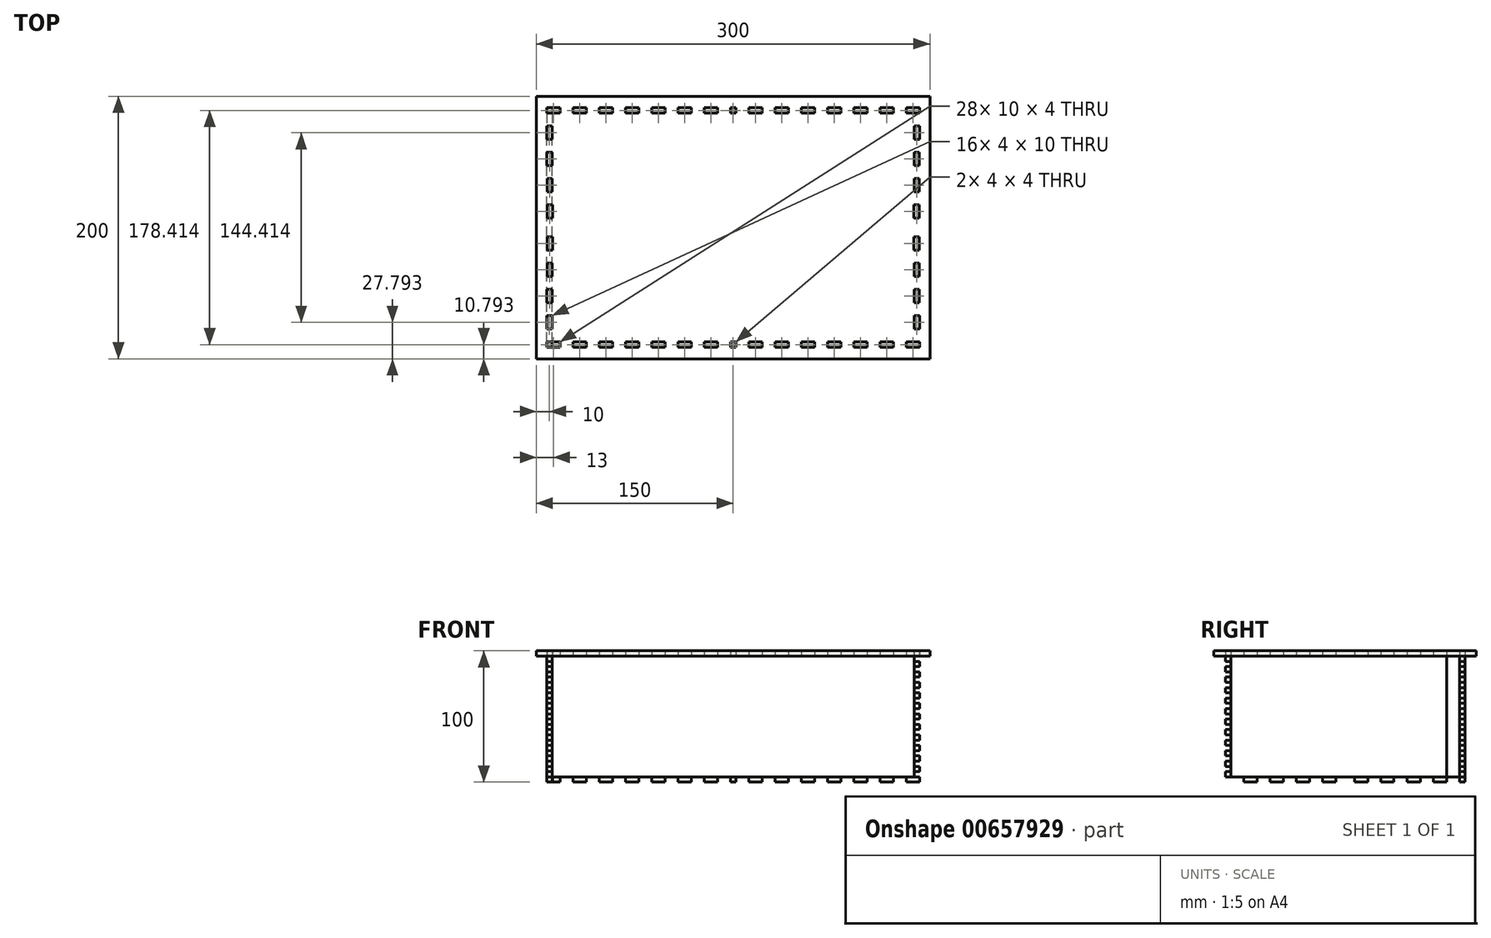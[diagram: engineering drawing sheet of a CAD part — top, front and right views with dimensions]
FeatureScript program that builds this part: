
annotation { "Feature Type Name" : "Feature", "Feature Type Description" : "" }
export const myFeature = defineFeature(function(context is Context, id is Id, definition is map)
    precondition{}
    {
        {
            assignVariable(context, id + "F0", {"name" : "width", "anyValue" : 4 * mm});
        }
        {
            var Q0;
            Q0=qCreatedBy(makeId("Top.planeOp"),FACE);
            var sketch = newSketch(context, id + "F1", { "sketchPlane" : qUnion([Q0])});
            skLineSegment(sketch, "E0.bottom", {"start": v(150, 100) * mm, "end": v(-150, 100) * mm});
            skLineSegment(sketch, "E0.top", {"start": v(150, -100) * mm, "end": v(-150, -100) * mm});
            skLineSegment(sketch, "E0.left", {"start": v(150, 100) * mm, "end": v(150, -100) * mm});
            skLineSegment(sketch, "E0.right", {"start": v(-150, 100) * mm, "end": v(-150, -100) * mm});
            skPoint(sketch, "E0.middle", {"position": v(0, 0) * mm});
            skLineSegment(sketch, "E1.bottom", {"start": v(-142, 87.2) * mm, "end": v(-132, 87.2) * mm});
            skLineSegment(sketch, "E1.top", {"start": v(-142, 91.2) * mm, "end": v(-132, 91.2) * mm});
            skLineSegment(sketch, "E1.left", {"start": v(-142, 87.2) * mm, "end": v(-142, 91.2) * mm});
            skLineSegment(sketch, "E1.right", {"start": v(-132, 87.2) * mm, "end": v(-132, 91.2) * mm});
            skLineSegment(sketch, "E2.1.0.0", {"start": v(-122, 91.2) * mm, "end": v(-112, 91.2) * mm});
            skLineSegment(sketch, "E2.1.0.1", {"start": v(-112, 87.2) * mm, "end": v(-112, 91.2) * mm});
            skLineSegment(sketch, "E2.1.0.2", {"start": v(-122, 87.2) * mm, "end": v(-122, 91.2) * mm});
            skLineSegment(sketch, "E2.1.0.3", {"start": v(-122, 87.2) * mm, "end": v(-112, 87.2) * mm});
            skLineSegment(sketch, "E2.2.0.0", {"start": v(-102, 91.2) * mm, "end": v(-92, 91.2) * mm});
            skLineSegment(sketch, "E2.2.0.1", {"start": v(-92, 87.2) * mm, "end": v(-92, 91.2) * mm});
            skLineSegment(sketch, "E2.2.0.2", {"start": v(-102, 87.2) * mm, "end": v(-102, 91.2) * mm});
            skLineSegment(sketch, "E2.2.0.3", {"start": v(-102, 87.2) * mm, "end": v(-92, 87.2) * mm});
            skLineSegment(sketch, "E2.3.0.0", {"start": v(-82, 91.2) * mm, "end": v(-72, 91.2) * mm});
            skLineSegment(sketch, "E2.3.0.1", {"start": v(-72, 87.2) * mm, "end": v(-72, 91.2) * mm});
            skLineSegment(sketch, "E2.3.0.2", {"start": v(-82, 87.2) * mm, "end": v(-82, 91.2) * mm});
            skLineSegment(sketch, "E2.3.0.3", {"start": v(-82, 87.2) * mm, "end": v(-72, 87.2) * mm});
            skLineSegment(sketch, "E2.4.0.0", {"start": v(-62, 91.2) * mm, "end": v(-52, 91.2) * mm});
            skLineSegment(sketch, "E2.4.0.1", {"start": v(-52, 87.2) * mm, "end": v(-52, 91.2) * mm});
            skLineSegment(sketch, "E2.4.0.2", {"start": v(-62, 87.2) * mm, "end": v(-62, 91.2) * mm});
            skLineSegment(sketch, "E2.4.0.3", {"start": v(-62, 87.2) * mm, "end": v(-52, 87.2) * mm});
            skLineSegment(sketch, "E2.5.0.0", {"start": v(-42, 91.2) * mm, "end": v(-32, 91.2) * mm});
            skLineSegment(sketch, "E2.5.0.1", {"start": v(-32, 87.2) * mm, "end": v(-32, 91.2) * mm});
            skLineSegment(sketch, "E2.5.0.2", {"start": v(-42, 87.2) * mm, "end": v(-42, 91.2) * mm});
            skLineSegment(sketch, "E2.5.0.3", {"start": v(-42, 87.2) * mm, "end": v(-32, 87.2) * mm});
            skLineSegment(sketch, "E2.6.0.0", {"start": v(-22, 91.2) * mm, "end": v(-12, 91.2) * mm});
            skLineSegment(sketch, "E2.6.0.1", {"start": v(-12, 87.2) * mm, "end": v(-12, 91.2) * mm});
            skLineSegment(sketch, "E2.6.0.2", {"start": v(-22, 87.2) * mm, "end": v(-22, 91.2) * mm});
            skLineSegment(sketch, "E2.6.0.3", {"start": v(-22, 87.2) * mm, "end": v(-12, 87.2) * mm});
            skLineSegment(sketch, "E2.7.0.0", {"start": v(-2, 91.2) * mm, "end": v(0, 91.2) * mm});
            skLineSegment(sketch, "E2.7.0.2", {"start": v(-2, 87.2) * mm, "end": v(-2, 91.2) * mm});
            skLineSegment(sketch, "E2.direction1", {"start": v(-142, 91.2) * mm, "end": v(-122, 91.2) * mm, "construction": true});
            skLineSegment(sketch, "E3", {"start": v(0, 0) * mm, "end": v(0, 100) * mm, "construction": true});
            skLineSegment(sketch, "E4", {"start": v(0, 0) * mm, "end": v(0, -100) * mm, "construction": true});
            skLineSegment(sketch, "E5.MirrorCS", {"start": v(142, 91.2) * mm, "end": v(132, 91.2) * mm});
            skLineSegment(sketch, "E6.MirrorCS", {"start": v(142, 87.2) * mm, "end": v(142, 91.2) * mm});
            skLineSegment(sketch, "E7.MirrorCS", {"start": v(142, 87.2) * mm, "end": v(132, 87.2) * mm});
            skLineSegment(sketch, "E8.MirrorCS", {"start": v(132, 87.2) * mm, "end": v(132, 91.2) * mm});
            skLineSegment(sketch, "E9.MirrorCS", {"start": v(62, 87.2) * mm, "end": v(62, 91.2) * mm});
            skLineSegment(sketch, "E10.MirrorCS", {"start": v(62, 91.2) * mm, "end": v(52, 91.2) * mm});
            skLineSegment(sketch, "E11.MirrorCS", {"start": v(52, 87.2) * mm, "end": v(52, 91.2) * mm});
            skLineSegment(sketch, "E12.MirrorCS", {"start": v(42, 87.2) * mm, "end": v(42, 91.2) * mm});
            skLineSegment(sketch, "E13.MirrorCS", {"start": v(42, 91.2) * mm, "end": v(32, 91.2) * mm});
            skLineSegment(sketch, "E14.MirrorCS", {"start": v(32, 87.2) * mm, "end": v(32, 91.2) * mm});
            skLineSegment(sketch, "E15.MirrorCS", {"start": v(2, 87.2) * mm, "end": v(2, 91.2) * mm});
            skLineSegment(sketch, "E16.MirrorCS", {"start": v(2, 91.2) * mm, "end": v(0, 91.2) * mm});
            skLineSegment(sketch, "E17.MirrorCS", {"start": v(12, 87.2) * mm, "end": v(12, 91.2) * mm});
            skLineSegment(sketch, "E18.MirrorCS", {"start": v(22, 87.2) * mm, "end": v(22, 91.2) * mm});
            skLineSegment(sketch, "E19.MirrorCS", {"start": v(22, 91.2) * mm, "end": v(12, 91.2) * mm});
            skLineSegment(sketch, "E20.MirrorCS", {"start": v(82, 91.2) * mm, "end": v(72, 91.2) * mm});
            skLineSegment(sketch, "E21.MirrorCS", {"start": v(102, 91.2) * mm, "end": v(92, 91.2) * mm});
            skLineSegment(sketch, "E22.MirrorCS", {"start": v(92, 87.2) * mm, "end": v(92, 91.2) * mm});
            skLineSegment(sketch, "E23.MirrorCS", {"start": v(102, 87.2) * mm, "end": v(102, 91.2) * mm});
            skLineSegment(sketch, "E24.MirrorCS", {"start": v(72, 87.2) * mm, "end": v(72, 91.2) * mm});
            skLineSegment(sketch, "E25.MirrorCS", {"start": v(82, 87.2) * mm, "end": v(82, 91.2) * mm});
            skLineSegment(sketch, "E26.MirrorCS", {"start": v(112, 87.2) * mm, "end": v(112, 91.2) * mm});
            skLineSegment(sketch, "E27.MirrorCS", {"start": v(122, 91.2) * mm, "end": v(112, 91.2) * mm});
            skLineSegment(sketch, "E28.MirrorCS", {"start": v(122, 87.2) * mm, "end": v(122, 91.2) * mm});
            skLineSegment(sketch, "E29", {"start": v(2, 87.2) * mm, "end": v(-2, 87.2) * mm});
            skLineSegment(sketch, "E30.MirrorCS", {"start": v(22, 87.2) * mm, "end": v(12, 87.2) * mm});
            skLineSegment(sketch, "E31.MirrorCS", {"start": v(102, 87.2) * mm, "end": v(92, 87.2) * mm});
            skLineSegment(sketch, "E32.MirrorCS", {"start": v(62, 87.2) * mm, "end": v(52, 87.2) * mm});
            skLineSegment(sketch, "E33.MirrorCS", {"start": v(82, 87.2) * mm, "end": v(72, 87.2) * mm});
            skLineSegment(sketch, "E34.MirrorCS", {"start": v(42, 87.2) * mm, "end": v(32, 87.2) * mm});
            skLineSegment(sketch, "E35.MirrorCS", {"start": v(122, 87.2) * mm, "end": v(112, 87.2) * mm});
            skLineSegment(sketch, "E36", {"start": v(150, 0) * mm, "end": v(-150, 0) * mm, "construction": true});
            skLineSegment(sketch, "E37.MirrorCS", {"start": v(42, -87.2) * mm, "end": v(42, -91.2) * mm});
            skLineSegment(sketch, "E38.MirrorCS", {"start": v(52, -87.2) * mm, "end": v(52, -91.2) * mm});
            skLineSegment(sketch, "E39.MirrorCS", {"start": v(32, -87.2) * mm, "end": v(32, -91.2) * mm});
            skLineSegment(sketch, "E40.MirrorCS", {"start": v(62, -87.2) * mm, "end": v(62, -91.2) * mm});
            skLineSegment(sketch, "E41.MirrorCS", {"start": v(92, -87.2) * mm, "end": v(92, -91.2) * mm});
            skLineSegment(sketch, "E42.MirrorCS", {"start": v(102, -87.2) * mm, "end": v(102, -91.2) * mm});
            skLineSegment(sketch, "E43.MirrorCS", {"start": v(132, -87.2) * mm, "end": v(132, -91.2) * mm});
            skLineSegment(sketch, "E44.MirrorCS", {"start": v(12, -87.2) * mm, "end": v(12, -91.2) * mm});
            skLineSegment(sketch, "E45.MirrorCS", {"start": v(72, -87.2) * mm, "end": v(72, -91.2) * mm});
            skLineSegment(sketch, "E46.MirrorCS", {"start": v(82, -87.2) * mm, "end": v(82, -91.2) * mm});
            skLineSegment(sketch, "E47.MirrorCS", {"start": v(22, -87.2) * mm, "end": v(22, -91.2) * mm});
            skLineSegment(sketch, "E48.MirrorCS", {"start": v(42, -91.2) * mm, "end": v(32, -91.2) * mm});
            skLineSegment(sketch, "E49.MirrorCS", {"start": v(-142, -87.2) * mm, "end": v(-142, -91.2) * mm});
            skLineSegment(sketch, "E50.MirrorCS", {"start": v(-122, -87.2) * mm, "end": v(-122, -91.2) * mm});
            skLineSegment(sketch, "E51.MirrorCS", {"start": v(-42, -87.2) * mm, "end": v(-42, -91.2) * mm});
            skLineSegment(sketch, "E52.MirrorCS", {"start": v(112, -87.2) * mm, "end": v(112, -91.2) * mm});
            skLineSegment(sketch, "E53.MirrorCS", {"start": v(-32, -87.2) * mm, "end": v(-32, -91.2) * mm});
            skLineSegment(sketch, "E54.MirrorCS", {"start": v(2, -87.2) * mm, "end": v(-2, -87.2) * mm});
            skLineSegment(sketch, "E55.MirrorCS", {"start": v(-12, -87.2) * mm, "end": v(-12, -91.2) * mm});
            skLineSegment(sketch, "E56.MirrorCS", {"start": v(-142, -91.2) * mm, "end": v(-132, -91.2) * mm});
            skLineSegment(sketch, "E57.MirrorCS", {"start": v(-2, -87.2) * mm, "end": v(-2, -91.2) * mm});
            skLineSegment(sketch, "E58.MirrorCS", {"start": v(-72, -87.2) * mm, "end": v(-72, -91.2) * mm});
            skLineSegment(sketch, "E59.MirrorCS", {"start": v(-132, -87.2) * mm, "end": v(-132, -91.2) * mm});
            skLineSegment(sketch, "E60.MirrorCS", {"start": v(-92, -87.2) * mm, "end": v(-92, -91.2) * mm});
            skLineSegment(sketch, "E61.MirrorCS", {"start": v(-52, -87.2) * mm, "end": v(-52, -91.2) * mm});
            skLineSegment(sketch, "E62.MirrorCS", {"start": v(-112, -87.2) * mm, "end": v(-112, -91.2) * mm});
            skLineSegment(sketch, "E63.MirrorCS", {"start": v(62, -91.2) * mm, "end": v(52, -91.2) * mm});
            skLineSegment(sketch, "E64.MirrorCS", {"start": v(-102, -87.2) * mm, "end": v(-102, -91.2) * mm});
            skLineSegment(sketch, "E65.MirrorCS", {"start": v(-82, -87.2) * mm, "end": v(-82, -91.2) * mm});
            skLineSegment(sketch, "E66.MirrorCS", {"start": v(2, -91.2) * mm, "end": v(0, -91.2) * mm});
            skLineSegment(sketch, "E67.MirrorCS", {"start": v(-62, -87.2) * mm, "end": v(-62, -91.2) * mm});
            skLineSegment(sketch, "E68.MirrorCS", {"start": v(-2, -91.2) * mm, "end": v(0, -91.2) * mm});
            skLineSegment(sketch, "E69.MirrorCS", {"start": v(122, -87.2) * mm, "end": v(122, -91.2) * mm});
            skLineSegment(sketch, "E70.MirrorCS", {"start": v(2, -87.2) * mm, "end": v(2, -91.2) * mm});
            skLineSegment(sketch, "E71.MirrorCS", {"start": v(-22, -87.2) * mm, "end": v(-22, -91.2) * mm});
            skLineSegment(sketch, "E72.MirrorCS", {"start": v(102, -91.2) * mm, "end": v(92, -91.2) * mm});
            skLineSegment(sketch, "E73.MirrorCS", {"start": v(-142, -91.2) * mm, "end": v(-122, -91.2) * mm, "construction": true});
            skLineSegment(sketch, "E74.MirrorCS", {"start": v(22, -91.2) * mm, "end": v(12, -91.2) * mm});
            skLineSegment(sketch, "E75.MirrorCS", {"start": v(82, -91.2) * mm, "end": v(72, -91.2) * mm});
            skLineSegment(sketch, "E76.MirrorCS", {"start": v(142, -91.2) * mm, "end": v(132, -91.2) * mm});
            skLineSegment(sketch, "E77.MirrorCS", {"start": v(-142, -87.2) * mm, "end": v(-132, -87.2) * mm});
            skLineSegment(sketch, "E78.MirrorCS", {"start": v(142, -87.2) * mm, "end": v(142, -91.2) * mm});
            skLineSegment(sketch, "E79.MirrorCS", {"start": v(142, -87.2) * mm, "end": v(132, -87.2) * mm});
            skLineSegment(sketch, "E80.MirrorCS", {"start": v(-82, -87.2) * mm, "end": v(-72, -87.2) * mm});
            skLineSegment(sketch, "E81.MirrorCS", {"start": v(82, -87.2) * mm, "end": v(72, -87.2) * mm});
            skLineSegment(sketch, "E82.MirrorCS", {"start": v(42, -87.2) * mm, "end": v(32, -87.2) * mm});
            skLineSegment(sketch, "E83.MirrorCS", {"start": v(122, -91.2) * mm, "end": v(112, -91.2) * mm});
            skLineSegment(sketch, "E84.MirrorCS", {"start": v(-62, -91.2) * mm, "end": v(-52, -91.2) * mm});
            skLineSegment(sketch, "E85.MirrorCS", {"start": v(122, -87.2) * mm, "end": v(112, -87.2) * mm});
            skLineSegment(sketch, "E86.MirrorCS", {"start": v(-42, -87.2) * mm, "end": v(-32, -87.2) * mm});
            skLineSegment(sketch, "E87.MirrorCS", {"start": v(-122, -91.2) * mm, "end": v(-112, -91.2) * mm});
            skLineSegment(sketch, "E88.MirrorCS", {"start": v(-102, -87.2) * mm, "end": v(-92, -87.2) * mm});
            skLineSegment(sketch, "E89.MirrorCS", {"start": v(-22, -87.2) * mm, "end": v(-12, -87.2) * mm});
            skLineSegment(sketch, "E90.MirrorCS", {"start": v(-102, -91.2) * mm, "end": v(-92, -91.2) * mm});
            skLineSegment(sketch, "E91.MirrorCS", {"start": v(-42, -91.2) * mm, "end": v(-32, -91.2) * mm});
            skLineSegment(sketch, "E92.MirrorCS", {"start": v(102, -87.2) * mm, "end": v(92, -87.2) * mm});
            skLineSegment(sketch, "E93.MirrorCS", {"start": v(-22, -91.2) * mm, "end": v(-12, -91.2) * mm});
            skLineSegment(sketch, "E94.MirrorCS", {"start": v(62, -87.2) * mm, "end": v(52, -87.2) * mm});
            skLineSegment(sketch, "E95.MirrorCS", {"start": v(-62, -87.2) * mm, "end": v(-52, -87.2) * mm});
            skLineSegment(sketch, "E96.MirrorCS", {"start": v(22, -87.2) * mm, "end": v(12, -87.2) * mm});
            skLineSegment(sketch, "E97.MirrorCS", {"start": v(-82, -91.2) * mm, "end": v(-72, -91.2) * mm});
            skLineSegment(sketch, "E98.MirrorCS", {"start": v(-122, -87.2) * mm, "end": v(-112, -87.2) * mm});
            skLineSegment(sketch, "E99.bottom", {"start": v(142, 77.2) * mm, "end": v(138, 77.2) * mm});
            skLineSegment(sketch, "E99.top", {"start": v(142, 67.2) * mm, "end": v(138, 67.2) * mm});
            skLineSegment(sketch, "E99.left", {"start": v(142, 77.2) * mm, "end": v(142, 67.2) * mm});
            skLineSegment(sketch, "E99.right", {"start": v(138, 77.2) * mm, "end": v(138, 67.2) * mm});
            skLineSegment(sketch, "E100.1.0.0", {"start": v(141.92, 47.2) * mm, "end": v(137.92, 47.2) * mm});
            skLineSegment(sketch, "E100.1.0.1", {"start": v(137.92, 57.2) * mm, "end": v(137.92, 47.2) * mm});
            skLineSegment(sketch, "E100.1.0.2", {"start": v(141.92, 57.2) * mm, "end": v(141.92, 47.2) * mm});
            skLineSegment(sketch, "E100.1.0.3", {"start": v(141.92, 57.2) * mm, "end": v(137.92, 57.2) * mm});
            skLineSegment(sketch, "E100.2.0.0", {"start": v(141.84, 27.2) * mm, "end": v(137.84, 27.2) * mm});
            skLineSegment(sketch, "E100.2.0.1", {"start": v(137.84, 37.2) * mm, "end": v(137.84, 27.2) * mm});
            skLineSegment(sketch, "E100.2.0.2", {"start": v(141.84, 37.2) * mm, "end": v(141.84, 27.2) * mm});
            skLineSegment(sketch, "E100.2.0.3", {"start": v(141.84, 37.2) * mm, "end": v(137.84, 37.2) * mm});
            skLineSegment(sketch, "E100.direction1", {"start": v(138, 67.2) * mm, "end": v(137.92, 47.2) * mm, "construction": true});
            skLineSegment(sketch, "E101.MirrorCS", {"start": v(141.84, -37.2) * mm, "end": v(141.84, -27.2) * mm});
            skLineSegment(sketch, "E102.MirrorCS", {"start": v(141.84, -37.2) * mm, "end": v(137.84, -37.2) * mm});
            skLineSegment(sketch, "E103.MirrorCS", {"start": v(137.84, -37.2) * mm, "end": v(137.84, -27.2) * mm});
            skLineSegment(sketch, "E104.MirrorCS", {"start": v(141.84, -27.2) * mm, "end": v(137.84, -27.2) * mm});
            skLineSegment(sketch, "E105.MirrorCS", {"start": v(141.92, -47.2) * mm, "end": v(137.92, -47.2) * mm});
            skLineSegment(sketch, "E106.MirrorCS", {"start": v(141.92, -57.2) * mm, "end": v(141.92, -47.2) * mm});
            skLineSegment(sketch, "E107.MirrorCS", {"start": v(141.92, -57.2) * mm, "end": v(137.92, -57.2) * mm});
            skLineSegment(sketch, "E108.MirrorCS", {"start": v(142, -67.2) * mm, "end": v(138, -67.2) * mm});
            skLineSegment(sketch, "E109.MirrorCS", {"start": v(142, -77.2) * mm, "end": v(142, -67.2) * mm});
            skLineSegment(sketch, "E110.MirrorCS", {"start": v(142, -77.2) * mm, "end": v(138, -77.2) * mm});
            skLineSegment(sketch, "E111.MirrorCS", {"start": v(138, -77.2) * mm, "end": v(138, -67.2) * mm});
            skLineSegment(sketch, "E112.MirrorCS", {"start": v(137.92, -57.2) * mm, "end": v(137.92, -47.2) * mm});
            skLineSegment(sketch, "E113.0.3.0", {"start": v(141.75, 7.2) * mm, "end": v(137.75, 7.2) * mm});
            skLineSegment(sketch, "E113.3.3.0", {"start": v(137.75, 17.2) * mm, "end": v(137.75, 7.2) * mm});
            skLineSegment(sketch, "E113.6.3.0", {"start": v(141.75, 17.2) * mm, "end": v(141.75, 7.2) * mm});
            skLineSegment(sketch, "E113.9.3.0", {"start": v(141.75, 17.2) * mm, "end": v(137.75, 17.2) * mm});
            skLineSegment(sketch, "E114.MirrorCS", {"start": v(141.75, -7.2) * mm, "end": v(137.75, -7.2) * mm});
            skLineSegment(sketch, "E115.MirrorCS", {"start": v(141.75, -17.2) * mm, "end": v(141.75, -7.2) * mm});
            skLineSegment(sketch, "E116.MirrorCS", {"start": v(137.75, -17.2) * mm, "end": v(137.75, -7.2) * mm});
            skLineSegment(sketch, "E117.MirrorCS", {"start": v(141.75, -17.2) * mm, "end": v(137.75, -17.2) * mm});
            skLineSegment(sketch, "E118", {"start": v(0, 100) * mm, "end": v(0, -100) * mm, "construction": true});
            skLineSegment(sketch, "E119.MirrorCS", {"start": v(-138, 77.2) * mm, "end": v(-138, 67.2) * mm});
            skLineSegment(sketch, "E120.MirrorCS", {"start": v(-142, 77.2) * mm, "end": v(-138, 77.2) * mm});
            skLineSegment(sketch, "E121.MirrorCS", {"start": v(-142, 77.2) * mm, "end": v(-142, 67.2) * mm});
            skLineSegment(sketch, "E122.MirrorCS", {"start": v(-142, 67.2) * mm, "end": v(-138, 67.2) * mm});
            skLineSegment(sketch, "E123.MirrorCS", {"start": v(-141.92, 57.2) * mm, "end": v(-141.92, 47.2) * mm});
            skLineSegment(sketch, "E124.MirrorCS", {"start": v(-137.92, 57.2) * mm, "end": v(-137.92, 47.2) * mm});
            skLineSegment(sketch, "E125.MirrorCS", {"start": v(-141.92, 57.2) * mm, "end": v(-137.92, 57.2) * mm});
            skLineSegment(sketch, "E126.MirrorCS", {"start": v(-141.92, 47.2) * mm, "end": v(-137.92, 47.2) * mm});
            skLineSegment(sketch, "E127.MirrorCS", {"start": v(-141.84, 37.2) * mm, "end": v(-137.84, 37.2) * mm});
            skLineSegment(sketch, "E128.MirrorCS", {"start": v(-141.84, 37.2) * mm, "end": v(-141.84, 27.2) * mm});
            skLineSegment(sketch, "E129.MirrorCS", {"start": v(-137.84, 37.2) * mm, "end": v(-137.84, 27.2) * mm});
            skLineSegment(sketch, "E130.MirrorCS", {"start": v(-141.84, 27.2) * mm, "end": v(-137.84, 27.2) * mm});
            skLineSegment(sketch, "E131.MirrorCS", {"start": v(-141.75, 17.2) * mm, "end": v(-137.75, 17.2) * mm});
            skLineSegment(sketch, "E132.MirrorCS", {"start": v(-137.75, 17.2) * mm, "end": v(-137.75, 7.2) * mm});
            skLineSegment(sketch, "E133.MirrorCS", {"start": v(-141.75, 17.2) * mm, "end": v(-141.75, 7.2) * mm});
            skLineSegment(sketch, "E134.MirrorCS", {"start": v(-141.75, 7.2) * mm, "end": v(-137.75, 7.2) * mm});
            skLineSegment(sketch, "E135.MirrorCS", {"start": v(-141.75, -17.2) * mm, "end": v(-137.75, -17.2) * mm});
            skLineSegment(sketch, "E136.MirrorCS", {"start": v(-142, -67.2) * mm, "end": v(-138, -67.2) * mm});
            skLineSegment(sketch, "E137.MirrorCS", {"start": v(-142, -77.2) * mm, "end": v(-138, -77.2) * mm});
            skLineSegment(sketch, "E138.MirrorCS", {"start": v(-141.92, -57.2) * mm, "end": v(-137.92, -57.2) * mm});
            skLineSegment(sketch, "E139.MirrorCS", {"start": v(-141.84, -27.2) * mm, "end": v(-137.84, -27.2) * mm});
            skLineSegment(sketch, "E140.MirrorCS", {"start": v(-141.75, -7.2) * mm, "end": v(-137.75, -7.2) * mm});
            skLineSegment(sketch, "E141.MirrorCS", {"start": v(-141.92, -47.2) * mm, "end": v(-137.92, -47.2) * mm});
            skLineSegment(sketch, "E142.MirrorCS", {"start": v(-141.84, -37.2) * mm, "end": v(-137.84, -37.2) * mm});
            skLineSegment(sketch, "E143.MirrorCS", {"start": v(-141.92, -57.2) * mm, "end": v(-141.92, -47.2) * mm});
            skLineSegment(sketch, "E144.MirrorCS", {"start": v(-142, -77.2) * mm, "end": v(-142, -67.2) * mm});
            skLineSegment(sketch, "E145.MirrorCS", {"start": v(-141.84, -37.2) * mm, "end": v(-141.84, -27.2) * mm});
            skLineSegment(sketch, "E146.MirrorCS", {"start": v(-137.84, -37.2) * mm, "end": v(-137.84, -27.2) * mm});
            skLineSegment(sketch, "E147.MirrorCS", {"start": v(-141.75, -17.2) * mm, "end": v(-141.75, -7.2) * mm});
            skLineSegment(sketch, "E148.MirrorCS", {"start": v(-138, -77.2) * mm, "end": v(-138, -67.2) * mm});
            skLineSegment(sketch, "E149.MirrorCS", {"start": v(-137.92, -57.2) * mm, "end": v(-137.92, -47.2) * mm});
            skLineSegment(sketch, "E150.MirrorCS", {"start": v(-137.75, -17.2) * mm, "end": v(-137.75, -7.2) * mm});
            skLineSegment(sketch, "E151", {"start": v(-138, 87.2) * mm, "end": v(-138, 91.2) * mm});
            skPoint(sketch, "E151.endSnap0", {"position": v(-137, 91.2) * mm});
            skSolve(sketch);
        }
        {
            var Q0;
            Q0=makeQuery(id+"F1.imprint","IMPRINT",FACE,{"disambiguationData":[TD([[makeQuery(id+"F1.imprint","IMPRINT",EDGE,{"derivedFrom":sQuery(id+"F1.wireOp",EDGE,"E0.bottom")}),1.0]])]});
            extrude(context, id + "F2", {"entities" : qUnion([Q0]), "depth" : 4 * mm});
        }
        {
            var Q0;
            Q0=makeQuery(id+"F1.imprint","IMPRINT",FACE,{"disambiguationData":[TD([[makeQuery(id+"F1.imprint","IMPRINT",EDGE,{"derivedFrom":sQuery(id+"F1.wireOp",EDGE,"E20.MirrorCS")}),1.0]])]});
            var Q1;
            Q1=makeQuery(id+"F1.imprint","IMPRINT",FACE,{"disambiguationData":[TD([[makeQuery(id+"F1.imprint","IMPRINT",EDGE,{"derivedFrom":sQuery(id+"F1.wireOp",EDGE,"E13.MirrorCS")}),1.0]])]});
            var Q2;
            Q2=makeQuery(id+"F1.imprint","IMPRINT",FACE,{"disambiguationData":[TD([[makeQuery(id+"F1.imprint","IMPRINT",EDGE,{"derivedFrom":sQuery(id+"F1.wireOp",EDGE,"E1.bottom")}),1.0]])]});
            var Q3;
            Q3=makeQuery(id+"F1.imprint","IMPRINT",FACE,{"disambiguationData":[TD([[makeQuery(id+"F1.imprint","IMPRINT",EDGE,{"derivedFrom":sQuery(id+"F1.wireOp",EDGE,"E2.1.0.0")}),-1.0]])]});
            var Q4;
            Q4=makeQuery(id+"F1.imprint","IMPRINT",FACE,{"disambiguationData":[TD([[makeQuery(id+"F1.imprint","IMPRINT",EDGE,{"derivedFrom":sQuery(id+"F1.wireOp",EDGE,"E2.2.0.0")}),-1.0]])]});
            var Q5;
            Q5=makeQuery(id+"F1.imprint","IMPRINT",FACE,{"disambiguationData":[TD([[makeQuery(id+"F1.imprint","IMPRINT",EDGE,{"derivedFrom":sQuery(id+"F1.wireOp",EDGE,"E2.3.0.0")}),-1.0]])]});
            var Q6;
            Q6=makeQuery(id+"F1.imprint","IMPRINT",FACE,{"disambiguationData":[TD([[makeQuery(id+"F1.imprint","IMPRINT",EDGE,{"derivedFrom":sQuery(id+"F1.wireOp",EDGE,"E2.4.0.0")}),-1.0]])]});
            var Q7;
            Q7=makeQuery(id+"F1.imprint","IMPRINT",FACE,{"disambiguationData":[TD([[makeQuery(id+"F1.imprint","IMPRINT",EDGE,{"derivedFrom":sQuery(id+"F1.wireOp",EDGE,"E2.5.0.0")}),-1.0]])]});
            var Q8;
            Q8=makeQuery(id+"F1.imprint","IMPRINT",FACE,{"disambiguationData":[TD([[makeQuery(id+"F1.imprint","IMPRINT",EDGE,{"derivedFrom":sQuery(id+"F1.wireOp",EDGE,"E2.6.0.0")}),-1.0]])]});
            var Q9;
            Q9=makeQuery(id+"F1.imprint","IMPRINT",FACE,{"disambiguationData":[TD([[makeQuery(id+"F1.imprint","IMPRINT",EDGE,{"derivedFrom":sQuery(id+"F1.wireOp",EDGE,"E6.MirrorCS")}),1.0]])]});
            var Q10;
            Q10=makeQuery(id+"F1.imprint","IMPRINT",FACE,{"disambiguationData":[TD([[makeQuery(id+"F1.imprint","IMPRINT",EDGE,{"derivedFrom":sQuery(id+"F1.wireOp",EDGE,"E26.MirrorCS")}),-1.0]])]});
            var Q11;
            Q11=makeQuery(id+"F1.imprint","IMPRINT",FACE,{"disambiguationData":[TD([[makeQuery(id+"F1.imprint","IMPRINT",EDGE,{"derivedFrom":sQuery(id+"F1.wireOp",EDGE,"E30.MirrorCS")}),-1.0]])]});
            var Q12;
            Q12=makeQuery(id+"F1.imprint","IMPRINT",FACE,{"disambiguationData":[TD([[makeQuery(id+"F1.imprint","IMPRINT",EDGE,{"derivedFrom":sQuery(id+"F1.wireOp",EDGE,"E31.MirrorCS")}),-1.0]])]});
            var Q13;
            Q13=makeQuery(id+"F1.imprint","IMPRINT",FACE,{"disambiguationData":[TD([[makeQuery(id+"F1.imprint","IMPRINT",EDGE,{"derivedFrom":sQuery(id+"F1.wireOp",EDGE,"E32.MirrorCS")}),-1.0]])]});
            var Q14;
            Q14=makeQuery(id+"F1.imprint","IMPRINT",FACE,{"disambiguationData":[TD([[makeQuery(id+"F1.imprint","IMPRINT",EDGE,{"derivedFrom":sQuery(id+"F1.wireOp",EDGE,"E2.7.0.0")}),-1.0]])]});
            extrude(context, id + "F3", {"entities" : qUnion([Q0, Q1, Q2, Q3, Q4, Q5, Q6, Q7, Q8, Q9, Q10, Q11, Q12, Q13, Q14]), "depth" : 4 * mm});
        }
        {
            var Q0;
            Q0=sQuery(id+"F1.wireOp",EDGE,"E151");
            extrude(context, id + "F4", {"bodyType" : ToolBodyType.SURFACE, "surfaceEntities" : qUnion([Q0]), "oppositeDirection" : true, "depth" : 92 * mm});
        }
        {
            var Q0;
            Q0=makeQuery(id+"F4.opExtrude","SWEPT_FACE",FACE,{"disambiguationData":[OSD([sQuery(id+"F1.wireOp",EDGE,"E151")])]});
            extrude(context, id + "F5", {"entities" : qUnion([Q0]), "oppositeDirection" : true, "depth" : 276 * mm});
        }
        {
            var Q0;
            Q0=makeQuery(id+"F1.imprint","IMPRINT",FACE,{"disambiguationData":[TD([[makeQuery(id+"F1.imprint","IMPRINT",EDGE,{"derivedFrom":sQuery(id+"F1.wireOp",EDGE,"E127.MirrorCS")}),-1.0]])]});
            var Q1;
            Q1=makeQuery(id+"F1.imprint","IMPRINT",FACE,{"disambiguationData":[TD([[makeQuery(id+"F1.imprint","IMPRINT",EDGE,{"derivedFrom":sQuery(id+"F1.wireOp",EDGE,"E123.MirrorCS")}),1.0]])]});
            var Q2;
            Q2=makeQuery(id+"F1.imprint","IMPRINT",FACE,{"disambiguationData":[TD([[makeQuery(id+"F1.imprint","IMPRINT",EDGE,{"derivedFrom":sQuery(id+"F1.wireOp",EDGE,"E119.MirrorCS")}),-1.0]])]});
            var Q3;
            Q3=makeQuery(id+"F1.imprint","IMPRINT",FACE,{"disambiguationData":[TD([[makeQuery(id+"F1.imprint","IMPRINT",EDGE,{"derivedFrom":sQuery(id+"F1.wireOp",EDGE,"E131.MirrorCS")}),-1.0]])]});
            var Q4;
            Q4=makeQuery(id+"F1.imprint","IMPRINT",FACE,{"disambiguationData":[TD([[makeQuery(id+"F1.imprint","IMPRINT",EDGE,{"derivedFrom":sQuery(id+"F1.wireOp",EDGE,"E138.MirrorCS")}),1.0]])]});
            var Q5;
            Q5=makeQuery(id+"F1.imprint","IMPRINT",FACE,{"disambiguationData":[TD([[makeQuery(id+"F1.imprint","IMPRINT",EDGE,{"derivedFrom":sQuery(id+"F1.wireOp",EDGE,"E136.MirrorCS")}),-1.0]])]});
            var Q6;
            Q6=makeQuery(id+"F1.imprint","IMPRINT",FACE,{"disambiguationData":[TD([[makeQuery(id+"F1.imprint","IMPRINT",EDGE,{"derivedFrom":sQuery(id+"F1.wireOp",EDGE,"E139.MirrorCS")}),-1.0]])]});
            var Q7;
            Q7=makeQuery(id+"F1.imprint","IMPRINT",FACE,{"disambiguationData":[TD([[makeQuery(id+"F1.imprint","IMPRINT",EDGE,{"derivedFrom":sQuery(id+"F1.wireOp",EDGE,"E135.MirrorCS")}),1.0]])]});
            extrude(context, id + "F6", {"entities" : qUnion([Q0, Q1, Q2, Q3, Q4, Q5, Q6, Q7]), "depth" : 4 * mm});
        }
        {
            var Q0;
            Q0=sQuery(id+"F1.wireOp",EDGE,"E120.MirrorCS");
            extrude(context, id + "F7", {"bodyType" : ToolBodyType.SURFACE, "surfaceEntities" : qUnion([Q0]), "oppositeDirection" : true, "depth" : 92 * mm});
        }
        {
            var Q0;
            Q0=makeQuery(id+"F7.opExtrude","SWEPT_FACE",FACE,{"disambiguationData":[OSD([sQuery(id+"F1.wireOp",EDGE,"E120.MirrorCS")])]});
            extrude(context, id + "F8", {"entities" : qUnion([Q0]), "oppositeDirection" : true, "depth" : 164.42 * mm});
        }
        {
            var Q0;
            Q0=makeQuery(id+"F7.opExtrude","SWEPT_FACE",FACE,{"disambiguationData":[OSD([sQuery(id+"F1.wireOp",EDGE,"E120.MirrorCS")])]});
            extrude(context, id + "F9", {"entities" : qUnion([Q0]), "depth" : 10 * mm});
        }
        {
            var Q0;
            Q0=makeQuery(id+"F1.imprint","IMPRINT",FACE,{"disambiguationData":[TD([[makeQuery(id+"F1.imprint","IMPRINT",EDGE,{"derivedFrom":sQuery(id+"F1.wireOp",EDGE,"E0.bottom")}),1.0]])]});
            cPlane(context, id + "F10", {"entities" : qUnion([Q0]), "cplaneType" : CPlaneType.OFFSET, "offset" : (92 / 2) * mm, "oppositeDirection" : true, "width" : 152.4 * mm, "height" : 152.4 * mm});
        }
        {
            var Q0;
            Q0=makeQuery(id+"F3.opExtrude","SWEPT_BODY",BODY,{"disambiguationData":[OSD([sQuery(id+"F1.wireOp",EDGE,"E6.MirrorCS"),sQuery(id+"F1.wireOp",EDGE,"E8.MirrorCS"),sQuery(id+"F1.wireOp",EDGE,"E5.MirrorCS"),sQuery(id+"F1.wireOp",EDGE,"E7.MirrorCS")])]});
            var Q1;
            Q1=makeQuery(id+"F3.opExtrude","SWEPT_BODY",BODY,{"disambiguationData":[OSD([sQuery(id+"F1.wireOp",EDGE,"E26.MirrorCS"),sQuery(id+"F1.wireOp",EDGE,"E27.MirrorCS"),sQuery(id+"F1.wireOp",EDGE,"E28.MirrorCS"),sQuery(id+"F1.wireOp",EDGE,"E35.MirrorCS")])]});
            var Q2;
            Q2=makeQuery(id+"F3.opExtrude","SWEPT_BODY",BODY,{"disambiguationData":[OSD([sQuery(id+"F1.wireOp",EDGE,"E31.MirrorCS"),sQuery(id+"F1.wireOp",EDGE,"E21.MirrorCS"),sQuery(id+"F1.wireOp",EDGE,"E23.MirrorCS"),sQuery(id+"F1.wireOp",EDGE,"E22.MirrorCS")])]});
            var Q3;
            Q3=makeQuery(id+"F3.opExtrude","SWEPT_BODY",BODY,{"disambiguationData":[OSD([sQuery(id+"F1.wireOp",EDGE,"E20.MirrorCS"),sQuery(id+"F1.wireOp",EDGE,"E33.MirrorCS"),sQuery(id+"F1.wireOp",EDGE,"E24.MirrorCS"),sQuery(id+"F1.wireOp",EDGE,"E25.MirrorCS")])]});
            var Q4;
            Q4=makeQuery(id+"F3.opExtrude","SWEPT_BODY",BODY,{"disambiguationData":[OSD([sQuery(id+"F1.wireOp",EDGE,"E32.MirrorCS"),sQuery(id+"F1.wireOp",EDGE,"E9.MirrorCS"),sQuery(id+"F1.wireOp",EDGE,"E11.MirrorCS"),sQuery(id+"F1.wireOp",EDGE,"E10.MirrorCS")])]});
            var Q5;
            Q5=makeQuery(id+"F3.opExtrude","SWEPT_BODY",BODY,{"disambiguationData":[OSD([sQuery(id+"F1.wireOp",EDGE,"E13.MirrorCS"),sQuery(id+"F1.wireOp",EDGE,"E34.MirrorCS"),sQuery(id+"F1.wireOp",EDGE,"E14.MirrorCS"),sQuery(id+"F1.wireOp",EDGE,"E12.MirrorCS")])]});
            var Q6;
            Q6=makeQuery(id+"F3.opExtrude","SWEPT_BODY",BODY,{"disambiguationData":[OSD([sQuery(id+"F1.wireOp",EDGE,"E30.MirrorCS"),sQuery(id+"F1.wireOp",EDGE,"E19.MirrorCS"),sQuery(id+"F1.wireOp",EDGE,"E18.MirrorCS"),sQuery(id+"F1.wireOp",EDGE,"E17.MirrorCS")])]});
            var Q7;
            Q7=makeQuery(id+"F3.opExtrude","SWEPT_BODY",BODY,{"disambiguationData":[OSD([sQuery(id+"F1.wireOp",EDGE,"E2.7.0.0"),sQuery(id+"F1.wireOp",EDGE,"E2.7.0.2"),sQuery(id+"F1.wireOp",EDGE,"E15.MirrorCS"),sQuery(id+"F1.wireOp",EDGE,"E16.MirrorCS"),sQuery(id+"F1.wireOp",EDGE,"E29")])]});
            var Q8;
            Q8=makeQuery(id+"F3.opExtrude","SWEPT_BODY",BODY,{"disambiguationData":[OSD([sQuery(id+"F1.wireOp",EDGE,"E2.6.0.0"),sQuery(id+"F1.wireOp",EDGE,"E2.6.0.1"),sQuery(id+"F1.wireOp",EDGE,"E2.6.0.2"),sQuery(id+"F1.wireOp",EDGE,"E2.6.0.3")])]});
            var Q9;
            Q9=makeQuery(id+"F3.opExtrude","SWEPT_BODY",BODY,{"disambiguationData":[OSD([sQuery(id+"F1.wireOp",EDGE,"E2.5.0.0"),sQuery(id+"F1.wireOp",EDGE,"E2.5.0.1"),sQuery(id+"F1.wireOp",EDGE,"E2.5.0.2"),sQuery(id+"F1.wireOp",EDGE,"E2.5.0.3")])]});
            var Q10;
            Q10=makeQuery(id+"F3.opExtrude","SWEPT_BODY",BODY,{"disambiguationData":[OSD([sQuery(id+"F1.wireOp",EDGE,"E2.4.0.0"),sQuery(id+"F1.wireOp",EDGE,"E2.4.0.1"),sQuery(id+"F1.wireOp",EDGE,"E2.4.0.2"),sQuery(id+"F1.wireOp",EDGE,"E2.4.0.3")])]});
            var Q11;
            Q11=makeQuery(id+"F3.opExtrude","SWEPT_BODY",BODY,{"disambiguationData":[OSD([sQuery(id+"F1.wireOp",EDGE,"E2.3.0.0"),sQuery(id+"F1.wireOp",EDGE,"E2.3.0.1"),sQuery(id+"F1.wireOp",EDGE,"E2.3.0.2"),sQuery(id+"F1.wireOp",EDGE,"E2.3.0.3")])]});
            var Q12;
            Q12=makeQuery(id+"F3.opExtrude","SWEPT_BODY",BODY,{"disambiguationData":[OSD([sQuery(id+"F1.wireOp",EDGE,"E2.2.0.0"),sQuery(id+"F1.wireOp",EDGE,"E2.2.0.1"),sQuery(id+"F1.wireOp",EDGE,"E2.2.0.2"),sQuery(id+"F1.wireOp",EDGE,"E2.2.0.3")])]});
            var Q13;
            Q13=makeQuery(id+"F3.opExtrude","SWEPT_BODY",BODY,{"disambiguationData":[OSD([sQuery(id+"F1.wireOp",EDGE,"E2.1.0.0"),sQuery(id+"F1.wireOp",EDGE,"E2.1.0.1"),sQuery(id+"F1.wireOp",EDGE,"E2.1.0.2"),sQuery(id+"F1.wireOp",EDGE,"E2.1.0.3")])]});
            var Q14;
            Q14=makeQuery(id+"F3.opExtrude","SWEPT_BODY",BODY,{"disambiguationData":[OSD([sQuery(id+"F1.wireOp",EDGE,"E1.bottom"),sQuery(id+"F1.wireOp",EDGE,"E1.top"),sQuery(id+"F1.wireOp",EDGE,"E1.left"),sQuery(id+"F1.wireOp",EDGE,"E1.right")])]});
            var Q15;
            Q15=makeQuery(id+"F6.opExtrude","SWEPT_BODY",BODY,{"disambiguationData":[OSD([sQuery(id+"F1.wireOp",EDGE,"E119.MirrorCS"),sQuery(id+"F1.wireOp",EDGE,"E120.MirrorCS"),sQuery(id+"F1.wireOp",EDGE,"E121.MirrorCS"),sQuery(id+"F1.wireOp",EDGE,"E122.MirrorCS")])]});
            var Q16;
            Q16=makeQuery(id+"F6.opExtrude","SWEPT_BODY",BODY,{"disambiguationData":[OSD([sQuery(id+"F1.wireOp",EDGE,"E123.MirrorCS"),sQuery(id+"F1.wireOp",EDGE,"E124.MirrorCS"),sQuery(id+"F1.wireOp",EDGE,"E125.MirrorCS"),sQuery(id+"F1.wireOp",EDGE,"E126.MirrorCS")])]});
            var Q17;
            Q17=makeQuery(id+"F6.opExtrude","SWEPT_BODY",BODY,{"disambiguationData":[OSD([sQuery(id+"F1.wireOp",EDGE,"E127.MirrorCS"),sQuery(id+"F1.wireOp",EDGE,"E128.MirrorCS"),sQuery(id+"F1.wireOp",EDGE,"E129.MirrorCS"),sQuery(id+"F1.wireOp",EDGE,"E130.MirrorCS")])]});
            var Q18;
            Q18=makeQuery(id+"F6.opExtrude","SWEPT_BODY",BODY,{"disambiguationData":[OSD([sQuery(id+"F1.wireOp",EDGE,"E131.MirrorCS"),sQuery(id+"F1.wireOp",EDGE,"E132.MirrorCS"),sQuery(id+"F1.wireOp",EDGE,"E133.MirrorCS"),sQuery(id+"F1.wireOp",EDGE,"E134.MirrorCS")])]});
            var Q19;
            Q19=makeQuery(id+"F6.opExtrude","SWEPT_BODY",BODY,{"disambiguationData":[OSD([sQuery(id+"F1.wireOp",EDGE,"E135.MirrorCS"),sQuery(id+"F1.wireOp",EDGE,"E140.MirrorCS"),sQuery(id+"F1.wireOp",EDGE,"E147.MirrorCS"),sQuery(id+"F1.wireOp",EDGE,"E150.MirrorCS")])]});
            var Q20;
            Q20=makeQuery(id+"F6.opExtrude","SWEPT_BODY",BODY,{"disambiguationData":[OSD([sQuery(id+"F1.wireOp",EDGE,"E139.MirrorCS"),sQuery(id+"F1.wireOp",EDGE,"E142.MirrorCS"),sQuery(id+"F1.wireOp",EDGE,"E145.MirrorCS"),sQuery(id+"F1.wireOp",EDGE,"E146.MirrorCS")])]});
            var Q21;
            Q21=makeQuery(id+"F6.opExtrude","SWEPT_BODY",BODY,{"disambiguationData":[OSD([sQuery(id+"F1.wireOp",EDGE,"E138.MirrorCS"),sQuery(id+"F1.wireOp",EDGE,"E141.MirrorCS"),sQuery(id+"F1.wireOp",EDGE,"E143.MirrorCS"),sQuery(id+"F1.wireOp",EDGE,"E149.MirrorCS")])]});
            var Q22;
            Q22=makeQuery(id+"F6.opExtrude","SWEPT_BODY",BODY,{"disambiguationData":[OSD([sQuery(id+"F1.wireOp",EDGE,"E136.MirrorCS"),sQuery(id+"F1.wireOp",EDGE,"E137.MirrorCS"),sQuery(id+"F1.wireOp",EDGE,"E144.MirrorCS"),sQuery(id+"F1.wireOp",EDGE,"E148.MirrorCS")])]});
            var Q23;
            Q23=qCreatedBy(id+"F10.planeOp",FACE);
            mirror(context, id + "F11", {"entities" : qUnion([Q0, Q1, Q2, Q3, Q4, Q5, Q6, Q7, Q8, Q9, Q10, Q11, Q12, Q13, Q14, Q15, Q16, Q17, Q18, Q19, Q20, Q21, Q22]), "mirrorPlane" : qUnion([Q23])});
        }
        {
            var Q0;
            Q0=makeQuery(id+"F5.opExtrude","CAP_FACE",FACE,{"disambiguationData":[OSD([sQuery(id+"F1.wireOp",EDGE,"E151")])],"isStart":false});
            var sketch = newSketch(context, id + "F12", { "sketchPlane" : qUnion([Q0])});
            skLineSegment(sketch, "E152.bottom", {"start": v(87.2, -92) * mm, "end": v(91.2, -92) * mm});
            skLineSegment(sketch, "E152.top", {"start": v(87.2, -96) * mm, "end": v(91.2, -96) * mm});
            skLineSegment(sketch, "E152.left", {"start": v(87.2, -92) * mm, "end": v(87.2, -96) * mm});
            skLineSegment(sketch, "E152.right", {"start": v(91.2, -92) * mm, "end": v(91.2, -96) * mm});
            skLineSegment(sketch, "E153.1.0.0", {"start": v(87.2, -84) * mm, "end": v(87.2, -88) * mm});
            skLineSegment(sketch, "E153.1.0.1", {"start": v(87.2, -84) * mm, "end": v(91.2, -84) * mm});
            skLineSegment(sketch, "E153.1.0.2", {"start": v(87.2, -88) * mm, "end": v(91.2, -88) * mm});
            skLineSegment(sketch, "E153.1.0.3", {"start": v(91.2, -84) * mm, "end": v(91.2, -88) * mm});
            skLineSegment(sketch, "E153.2.0.0", {"start": v(87.2, -76) * mm, "end": v(87.2, -80) * mm});
            skLineSegment(sketch, "E153.2.0.1", {"start": v(87.2, -76) * mm, "end": v(91.2, -76) * mm});
            skLineSegment(sketch, "E153.2.0.2", {"start": v(87.2, -80) * mm, "end": v(91.2, -80) * mm});
            skLineSegment(sketch, "E153.2.0.3", {"start": v(91.2, -76) * mm, "end": v(91.2, -80) * mm});
            skLineSegment(sketch, "E153.3.0.0", {"start": v(87.2, -68) * mm, "end": v(87.2, -72) * mm});
            skLineSegment(sketch, "E153.3.0.1", {"start": v(87.2, -68) * mm, "end": v(91.2, -68) * mm});
            skLineSegment(sketch, "E153.3.0.2", {"start": v(87.2, -72) * mm, "end": v(91.2, -72) * mm});
            skLineSegment(sketch, "E153.3.0.3", {"start": v(91.2, -68) * mm, "end": v(91.2, -72) * mm});
            skLineSegment(sketch, "E153.4.0.0", {"start": v(87.2, -60) * mm, "end": v(87.2, -64) * mm});
            skLineSegment(sketch, "E153.4.0.1", {"start": v(87.2, -60) * mm, "end": v(91.2, -60) * mm});
            skLineSegment(sketch, "E153.4.0.2", {"start": v(87.2, -64) * mm, "end": v(91.2, -64) * mm});
            skLineSegment(sketch, "E153.4.0.3", {"start": v(91.2, -60) * mm, "end": v(91.2, -64) * mm});
            skLineSegment(sketch, "E153.5.0.0", {"start": v(87.2, -52) * mm, "end": v(87.2, -56) * mm});
            skLineSegment(sketch, "E153.5.0.1", {"start": v(87.2, -52) * mm, "end": v(91.2, -52) * mm});
            skLineSegment(sketch, "E153.5.0.2", {"start": v(87.2, -56) * mm, "end": v(91.2, -56) * mm});
            skLineSegment(sketch, "E153.5.0.3", {"start": v(91.2, -52) * mm, "end": v(91.2, -56) * mm});
            skLineSegment(sketch, "E153.6.0.0", {"start": v(87.2, -44) * mm, "end": v(87.2, -48) * mm});
            skLineSegment(sketch, "E153.6.0.1", {"start": v(87.2, -44) * mm, "end": v(91.2, -44) * mm});
            skLineSegment(sketch, "E153.6.0.2", {"start": v(87.2, -48) * mm, "end": v(91.2, -48) * mm});
            skLineSegment(sketch, "E153.6.0.3", {"start": v(91.2, -44) * mm, "end": v(91.2, -48) * mm});
            skLineSegment(sketch, "E153.7.0.0", {"start": v(87.2, -36) * mm, "end": v(87.2, -40) * mm});
            skLineSegment(sketch, "E153.7.0.1", {"start": v(87.2, -36) * mm, "end": v(91.2, -36) * mm});
            skLineSegment(sketch, "E153.7.0.2", {"start": v(87.2, -40) * mm, "end": v(91.2, -40) * mm});
            skLineSegment(sketch, "E153.7.0.3", {"start": v(91.2, -36) * mm, "end": v(91.2, -40) * mm});
            skLineSegment(sketch, "E153.8.0.0", {"start": v(87.2, -28) * mm, "end": v(87.2, -32) * mm});
            skLineSegment(sketch, "E153.8.0.1", {"start": v(87.2, -28) * mm, "end": v(91.2, -28) * mm});
            skLineSegment(sketch, "E153.8.0.2", {"start": v(87.2, -32) * mm, "end": v(91.2, -32) * mm});
            skLineSegment(sketch, "E153.8.0.3", {"start": v(91.2, -28) * mm, "end": v(91.2, -32) * mm});
            skLineSegment(sketch, "E153.9.0.0", {"start": v(87.2, -20) * mm, "end": v(87.2, -24) * mm});
            skLineSegment(sketch, "E153.9.0.1", {"start": v(87.2, -20) * mm, "end": v(91.2, -20) * mm});
            skLineSegment(sketch, "E153.9.0.2", {"start": v(87.2, -24) * mm, "end": v(91.2, -24) * mm});
            skLineSegment(sketch, "E153.9.0.3", {"start": v(91.2, -20) * mm, "end": v(91.2, -24) * mm});
            skLineSegment(sketch, "E153.10.0.0", {"start": v(87.2, -12) * mm, "end": v(87.2, -16) * mm});
            skLineSegment(sketch, "E153.10.0.1", {"start": v(87.2, -12) * mm, "end": v(91.2, -12) * mm});
            skLineSegment(sketch, "E153.10.0.2", {"start": v(87.2, -16) * mm, "end": v(91.2, -16) * mm});
            skLineSegment(sketch, "E153.10.0.3", {"start": v(91.2, -12) * mm, "end": v(91.2, -16) * mm});
            skLineSegment(sketch, "E153.11.0.0", {"start": v(87.2, -4) * mm, "end": v(87.2, -8) * mm});
            skLineSegment(sketch, "E153.11.0.1", {"start": v(87.2, -4) * mm, "end": v(91.2, -4) * mm});
            skLineSegment(sketch, "E153.11.0.2", {"start": v(87.2, -8) * mm, "end": v(91.2, -8) * mm});
            skLineSegment(sketch, "E153.11.0.3", {"start": v(91.2, -4) * mm, "end": v(91.2, -8) * mm});
            skLineSegment(sketch, "E153.direction1", {"start": v(87.2, -96) * mm, "end": v(87.2, -88) * mm, "construction": true});
            skSolve(sketch);
        }
        {
            var Q0;
            Q0=makeQuery(id+"F12.imprint","IMPRINT",FACE,{"disambiguationData":[TD([[makeQuery(id+"F12.imprint","IMPRINT",EDGE,{"derivedFrom":sQuery(id+"F12.wireOp",EDGE,"E153.1.0.0")}),1.0]])]});
            var Q1;
            Q1=makeQuery(id+"F12.imprint","IMPRINT",FACE,{"disambiguationData":[TD([[makeQuery(id+"F12.imprint","IMPRINT",EDGE,{"derivedFrom":sQuery(id+"F12.wireOp",EDGE,"E153.2.0.0")}),1.0]])]});
            var Q2;
            Q2=makeQuery(id+"F12.imprint","IMPRINT",FACE,{"disambiguationData":[TD([[makeQuery(id+"F12.imprint","IMPRINT",EDGE,{"derivedFrom":sQuery(id+"F12.wireOp",EDGE,"E153.3.0.0")}),1.0]])]});
            var Q3;
            Q3=makeQuery(id+"F12.imprint","IMPRINT",FACE,{"disambiguationData":[TD([[makeQuery(id+"F12.imprint","IMPRINT",EDGE,{"derivedFrom":sQuery(id+"F12.wireOp",EDGE,"E153.4.0.0")}),1.0]])]});
            var Q4;
            Q4=makeQuery(id+"F12.imprint","IMPRINT",FACE,{"disambiguationData":[TD([[makeQuery(id+"F12.imprint","IMPRINT",EDGE,{"derivedFrom":sQuery(id+"F12.wireOp",EDGE,"E153.5.0.0")}),1.0]])]});
            var Q5;
            Q5=makeQuery(id+"F12.imprint","IMPRINT",FACE,{"disambiguationData":[TD([[makeQuery(id+"F12.imprint","IMPRINT",EDGE,{"derivedFrom":sQuery(id+"F12.wireOp",EDGE,"E153.6.0.0")}),1.0]])]});
            var Q6;
            Q6=makeQuery(id+"F12.imprint","IMPRINT",FACE,{"disambiguationData":[TD([[makeQuery(id+"F12.imprint","IMPRINT",EDGE,{"derivedFrom":sQuery(id+"F12.wireOp",EDGE,"E153.7.0.0")}),1.0]])]});
            var Q7;
            Q7=makeQuery(id+"F12.imprint","IMPRINT",FACE,{"disambiguationData":[TD([[makeQuery(id+"F12.imprint","IMPRINT",EDGE,{"derivedFrom":sQuery(id+"F12.wireOp",EDGE,"E153.8.0.0")}),1.0]])]});
            var Q8;
            Q8=makeQuery(id+"F12.imprint","IMPRINT",FACE,{"disambiguationData":[TD([[makeQuery(id+"F12.imprint","IMPRINT",EDGE,{"derivedFrom":sQuery(id+"F12.wireOp",EDGE,"E153.9.0.0")}),1.0]])]});
            var Q9;
            Q9=makeQuery(id+"F12.imprint","IMPRINT",FACE,{"disambiguationData":[TD([[makeQuery(id+"F12.imprint","IMPRINT",EDGE,{"derivedFrom":sQuery(id+"F12.wireOp",EDGE,"E153.10.0.0")}),1.0]])]});
            var Q10;
            {var subQ0=sQuery(id+"F12.wireOp",EDGE,"E153.11.0.0");Q10=makeQuery(id+"F12.imprint","IMPRINT",FACE,{"disambiguationData":[TD([[makeQuery(id+"F12.imprint","IMPRINT",EDGE,{"derivedFrom":subQ0}),1.0]])]});}
            extrude(context, id + "F13", {"entities" : qUnion([Q0, Q1, Q2, Q3, Q4, Q5, Q6, Q7, Q8, Q9, Q10]), "depth" : 4 * mm});
        }
        {
            var Q0;
            Q0=makeQuery(id+"F13.opExtrude","SWEPT_BODY",BODY,{"disambiguationData":[OSD([sQuery(id+"F12.wireOp",EDGE,"E153.8.0.0"),sQuery(id+"F12.wireOp",EDGE,"E153.8.0.1"),sQuery(id+"F12.wireOp",EDGE,"E153.8.0.2"),sQuery(id+"F12.wireOp",EDGE,"E153.8.0.3")])]});
            var Q1;
            Q1=makeQuery(id+"F13.opExtrude","SWEPT_BODY",BODY,{"disambiguationData":[OSD([sQuery(id+"F12.wireOp",EDGE,"E153.9.0.0"),sQuery(id+"F12.wireOp",EDGE,"E153.9.0.1"),sQuery(id+"F12.wireOp",EDGE,"E153.9.0.2"),sQuery(id+"F12.wireOp",EDGE,"E153.9.0.3")])]});
            var Q2;
            Q2=makeQuery(id+"F13.opExtrude","SWEPT_BODY",BODY,{"disambiguationData":[OSD([sQuery(id+"F12.wireOp",EDGE,"E153.2.0.0"),sQuery(id+"F12.wireOp",EDGE,"E153.2.0.1"),sQuery(id+"F12.wireOp",EDGE,"E153.2.0.2"),sQuery(id+"F12.wireOp",EDGE,"E153.2.0.3")])]});
            var Q3;
            Q3=makeQuery(id+"F13.opExtrude","SWEPT_BODY",BODY,{"disambiguationData":[OSD([sQuery(id+"F12.wireOp",EDGE,"E153.3.0.0"),sQuery(id+"F12.wireOp",EDGE,"E153.3.0.1"),sQuery(id+"F12.wireOp",EDGE,"E153.3.0.2"),sQuery(id+"F12.wireOp",EDGE,"E153.3.0.3")])]});
            var Q4;
            Q4=makeQuery(id+"F13.opExtrude","SWEPT_BODY",BODY,{"disambiguationData":[OSD([sQuery(id+"F12.wireOp",EDGE,"E153.10.0.0"),sQuery(id+"F12.wireOp",EDGE,"E153.10.0.1"),sQuery(id+"F12.wireOp",EDGE,"E153.10.0.2"),sQuery(id+"F12.wireOp",EDGE,"E153.10.0.3")])]});
            var Q5;
            Q5=makeQuery(id+"F13.opExtrude","SWEPT_BODY",BODY,{"disambiguationData":[OSD([sQuery(id+"F1.wireOp",VERTEX,"E1.left.end"),sQuery(id+"F12.wireOp",EDGE,"E153.11.0.0"),sQuery(id+"F12.wireOp",EDGE,"E153.11.0.1"),sQuery(id+"F12.wireOp",EDGE,"E153.11.0.2")])]});
            var Q6;
            Q6=makeQuery(id+"F13.opExtrude","SWEPT_BODY",BODY,{"disambiguationData":[OSD([sQuery(id+"F12.wireOp",EDGE,"E153.6.0.0"),sQuery(id+"F12.wireOp",EDGE,"E153.6.0.1"),sQuery(id+"F12.wireOp",EDGE,"E153.6.0.2"),sQuery(id+"F12.wireOp",EDGE,"E153.6.0.3")])]});
            var Q7;
            Q7=makeQuery(id+"F13.opExtrude","SWEPT_BODY",BODY,{"disambiguationData":[OSD([sQuery(id+"F12.wireOp",EDGE,"E153.5.0.0"),sQuery(id+"F12.wireOp",EDGE,"E153.5.0.1"),sQuery(id+"F12.wireOp",EDGE,"E153.5.0.2"),sQuery(id+"F12.wireOp",EDGE,"E153.5.0.3")])]});
            var Q8;
            Q8=makeQuery(id+"F13.opExtrude","SWEPT_BODY",BODY,{"disambiguationData":[OSD([sQuery(id+"F12.wireOp",EDGE,"E153.7.0.0"),sQuery(id+"F12.wireOp",EDGE,"E153.7.0.1"),sQuery(id+"F12.wireOp",EDGE,"E153.7.0.2"),sQuery(id+"F12.wireOp",EDGE,"E153.7.0.3")])]});
            var Q9;
            Q9=makeQuery(id+"F13.opExtrude","SWEPT_BODY",BODY,{"disambiguationData":[OSD([sQuery(id+"F12.wireOp",EDGE,"E153.1.0.0"),sQuery(id+"F12.wireOp",EDGE,"E153.1.0.1"),sQuery(id+"F12.wireOp",EDGE,"E153.1.0.2"),sQuery(id+"F12.wireOp",EDGE,"E153.1.0.3")])]});
            var Q10;
            Q10=makeQuery(id+"F13.opExtrude","SWEPT_BODY",BODY,{"disambiguationData":[OSD([sQuery(id+"F12.wireOp",EDGE,"E153.4.0.0"),sQuery(id+"F12.wireOp",EDGE,"E153.4.0.1"),sQuery(id+"F12.wireOp",EDGE,"E153.4.0.2"),sQuery(id+"F12.wireOp",EDGE,"E153.4.0.3")])]});
            var Q11;
            Q11=qCreatedBy(makeId("Right.planeOp"),FACE);
            mirror(context, id + "F14", {"entities" : qUnion([Q0, Q1, Q2, Q3, Q4, Q5, Q6, Q7, Q8, Q9, Q10]), "mirrorPlane" : qUnion([Q11])});
        }
        {
            var Q0;
            Q0=makeQuery(id+"F9.opExtrude","CAP_FACE",FACE,{"disambiguationData":[OSD([sQuery(id+"F1.wireOp",EDGE,"E120.MirrorCS")])],"isStart":false});
            var sketch = newSketch(context, id + "F15", { "sketchPlane" : qUnion([Q0])});
            skLineSegment(sketch, "E154.bottom", {"start": v(138, 0) * mm, "end": v(142, 0) * mm});
            skLineSegment(sketch, "E154.top", {"start": v(138, -4) * mm, "end": v(142, -4) * mm});
            skLineSegment(sketch, "E154.left", {"start": v(138, 0) * mm, "end": v(138, -4) * mm});
            skLineSegment(sketch, "E154.right", {"start": v(142, 0) * mm, "end": v(142, -4) * mm});
            skLineSegment(sketch, "E155.0.1.0", {"start": v(138, -12) * mm, "end": v(142, -12) * mm});
            skLineSegment(sketch, "E155.0.1.1", {"start": v(142, -8) * mm, "end": v(142, -12) * mm});
            skLineSegment(sketch, "E155.0.1.2", {"start": v(138, -8) * mm, "end": v(138, -12) * mm});
            skLineSegment(sketch, "E155.0.1.3", {"start": v(138, -8) * mm, "end": v(142, -8) * mm});
            skLineSegment(sketch, "E155.0.2.0", {"start": v(138, -20) * mm, "end": v(142, -20) * mm});
            skLineSegment(sketch, "E155.0.2.1", {"start": v(142, -16) * mm, "end": v(142, -20) * mm});
            skLineSegment(sketch, "E155.0.2.2", {"start": v(138, -16) * mm, "end": v(138, -20) * mm});
            skLineSegment(sketch, "E155.0.2.3", {"start": v(138, -16) * mm, "end": v(142, -16) * mm});
            skLineSegment(sketch, "E155.0.3.0", {"start": v(138, -28) * mm, "end": v(142, -28) * mm});
            skLineSegment(sketch, "E155.0.3.1", {"start": v(142, -24) * mm, "end": v(142, -28) * mm});
            skLineSegment(sketch, "E155.0.3.2", {"start": v(138, -24) * mm, "end": v(138, -28) * mm});
            skLineSegment(sketch, "E155.0.3.3", {"start": v(138, -24) * mm, "end": v(142, -24) * mm});
            skLineSegment(sketch, "E155.0.4.0", {"start": v(138, -36) * mm, "end": v(142, -36) * mm});
            skLineSegment(sketch, "E155.0.4.1", {"start": v(142, -32) * mm, "end": v(142, -36) * mm});
            skLineSegment(sketch, "E155.0.4.2", {"start": v(138, -32) * mm, "end": v(138, -36) * mm});
            skLineSegment(sketch, "E155.0.4.3", {"start": v(138, -32) * mm, "end": v(142, -32) * mm});
            skLineSegment(sketch, "E155.0.5.0", {"start": v(138, -44) * mm, "end": v(142, -44) * mm});
            skLineSegment(sketch, "E155.0.5.1", {"start": v(142, -40) * mm, "end": v(142, -44) * mm});
            skLineSegment(sketch, "E155.0.5.2", {"start": v(138, -40) * mm, "end": v(138, -44) * mm});
            skLineSegment(sketch, "E155.0.5.3", {"start": v(138, -40) * mm, "end": v(142, -40) * mm});
            skLineSegment(sketch, "E155.0.6.0", {"start": v(138, -52) * mm, "end": v(142, -52) * mm});
            skLineSegment(sketch, "E155.0.6.1", {"start": v(142, -48) * mm, "end": v(142, -52) * mm});
            skLineSegment(sketch, "E155.0.6.2", {"start": v(138, -48) * mm, "end": v(138, -52) * mm});
            skLineSegment(sketch, "E155.0.6.3", {"start": v(138, -48) * mm, "end": v(142, -48) * mm});
            skLineSegment(sketch, "E155.0.7.0", {"start": v(138, -60) * mm, "end": v(142, -60) * mm});
            skLineSegment(sketch, "E155.0.7.1", {"start": v(142, -56) * mm, "end": v(142, -60) * mm});
            skLineSegment(sketch, "E155.0.7.2", {"start": v(138, -56) * mm, "end": v(138, -60) * mm});
            skLineSegment(sketch, "E155.0.7.3", {"start": v(138, -56) * mm, "end": v(142, -56) * mm});
            skLineSegment(sketch, "E155.0.8.0", {"start": v(138, -68) * mm, "end": v(142, -68) * mm});
            skLineSegment(sketch, "E155.0.8.1", {"start": v(142, -64) * mm, "end": v(142, -68) * mm});
            skLineSegment(sketch, "E155.0.8.2", {"start": v(138, -64) * mm, "end": v(138, -68) * mm});
            skLineSegment(sketch, "E155.0.8.3", {"start": v(138, -64) * mm, "end": v(142, -64) * mm});
            skLineSegment(sketch, "E155.0.9.0", {"start": v(138, -76) * mm, "end": v(142, -76) * mm});
            skLineSegment(sketch, "E155.0.9.1", {"start": v(142, -72) * mm, "end": v(142, -76) * mm});
            skLineSegment(sketch, "E155.0.9.2", {"start": v(138, -72) * mm, "end": v(138, -76) * mm});
            skLineSegment(sketch, "E155.0.9.3", {"start": v(138, -72) * mm, "end": v(142, -72) * mm});
            skLineSegment(sketch, "E155.0.10.0", {"start": v(138, -84) * mm, "end": v(142, -84) * mm});
            skLineSegment(sketch, "E155.0.10.1", {"start": v(142, -80) * mm, "end": v(142, -84) * mm});
            skLineSegment(sketch, "E155.0.10.2", {"start": v(138, -80) * mm, "end": v(138, -84) * mm});
            skLineSegment(sketch, "E155.0.10.3", {"start": v(138, -80) * mm, "end": v(142, -80) * mm});
            skLineSegment(sketch, "E155.0.11.0", {"start": v(138, -92) * mm, "end": v(142, -92) * mm});
            skLineSegment(sketch, "E155.0.11.1", {"start": v(142, -88) * mm, "end": v(142, -92) * mm});
            skLineSegment(sketch, "E155.0.11.2", {"start": v(138, -88) * mm, "end": v(138, -92) * mm});
            skLineSegment(sketch, "E155.0.11.3", {"start": v(138, -88) * mm, "end": v(142, -88) * mm});
            skLineSegment(sketch, "E155.direction2", {"start": v(138, -4) * mm, "end": v(138, -12) * mm, "construction": true});
            skSolve(sketch);
        }
        {
            var Q0;
            Q0=qSketchRegion(id+"F15",true);
            extrude(context, id + "F16", {"entities" : qUnion([Q0]), "depth" : getVariable(context, 'width')});
        }
        {
            var Q0;
            Q0=makeQuery(id+"F16.opExtrude","SWEPT_BODY",BODY,{"disambiguationData":[OSD([sQuery(id+"F15.wireOp",EDGE,"E155.0.11.0"),sQuery(id+"F15.wireOp",EDGE,"E155.0.11.1"),sQuery(id+"F15.wireOp",EDGE,"E155.0.11.2"),sQuery(id+"F15.wireOp",EDGE,"E155.0.11.3")])]});
            var Q1;
            Q1=makeQuery(id+"F16.opExtrude","SWEPT_BODY",BODY,{"disambiguationData":[OSD([sQuery(id+"F15.wireOp",EDGE,"E155.0.5.0"),sQuery(id+"F15.wireOp",EDGE,"E155.0.5.1"),sQuery(id+"F15.wireOp",EDGE,"E155.0.5.2"),sQuery(id+"F15.wireOp",EDGE,"E155.0.5.3")])]});
            var Q2;
            Q2=makeQuery(id+"F16.opExtrude","SWEPT_BODY",BODY,{"disambiguationData":[OSD([sQuery(id+"F15.wireOp",EDGE,"E154.bottom"),sQuery(id+"F15.wireOp",EDGE,"E154.top"),sQuery(id+"F15.wireOp",EDGE,"E154.left"),sQuery(id+"F15.wireOp",EDGE,"E154.right")])]});
            var Q3;
            Q3=makeQuery(id+"F16.opExtrude","SWEPT_BODY",BODY,{"disambiguationData":[OSD([sQuery(id+"F15.wireOp",EDGE,"E155.0.1.0"),sQuery(id+"F15.wireOp",EDGE,"E155.0.1.1"),sQuery(id+"F15.wireOp",EDGE,"E155.0.1.2"),sQuery(id+"F15.wireOp",EDGE,"E155.0.1.3")])]});
            var Q4;
            Q4=makeQuery(id+"F16.opExtrude","SWEPT_BODY",BODY,{"disambiguationData":[OSD([sQuery(id+"F15.wireOp",EDGE,"E155.0.10.0"),sQuery(id+"F15.wireOp",EDGE,"E155.0.10.1"),sQuery(id+"F15.wireOp",EDGE,"E155.0.10.2"),sQuery(id+"F15.wireOp",EDGE,"E155.0.10.3")])]});
            var Q5;
            Q5=makeQuery(id+"F16.opExtrude","SWEPT_BODY",BODY,{"disambiguationData":[OSD([sQuery(id+"F15.wireOp",EDGE,"E155.0.2.0"),sQuery(id+"F15.wireOp",EDGE,"E155.0.2.1"),sQuery(id+"F15.wireOp",EDGE,"E155.0.2.2"),sQuery(id+"F15.wireOp",EDGE,"E155.0.2.3")])]});
            var Q6;
            Q6=makeQuery(id+"F16.opExtrude","SWEPT_BODY",BODY,{"disambiguationData":[OSD([sQuery(id+"F15.wireOp",EDGE,"E155.0.4.0"),sQuery(id+"F15.wireOp",EDGE,"E155.0.4.1"),sQuery(id+"F15.wireOp",EDGE,"E155.0.4.2"),sQuery(id+"F15.wireOp",EDGE,"E155.0.4.3")])]});
            var Q7;
            Q7=makeQuery(id+"F16.opExtrude","SWEPT_BODY",BODY,{"disambiguationData":[OSD([sQuery(id+"F15.wireOp",EDGE,"E155.0.6.0"),sQuery(id+"F15.wireOp",EDGE,"E155.0.6.1"),sQuery(id+"F15.wireOp",EDGE,"E155.0.6.2"),sQuery(id+"F15.wireOp",EDGE,"E155.0.6.3")])]});
            var Q8;
            Q8=makeQuery(id+"F16.opExtrude","SWEPT_BODY",BODY,{"disambiguationData":[OSD([sQuery(id+"F15.wireOp",EDGE,"E155.0.3.0"),sQuery(id+"F15.wireOp",EDGE,"E155.0.3.1"),sQuery(id+"F15.wireOp",EDGE,"E155.0.3.2"),sQuery(id+"F15.wireOp",EDGE,"E155.0.3.3")])]});
            var Q9;
            Q9=makeQuery(id+"F16.opExtrude","SWEPT_BODY",BODY,{"disambiguationData":[OSD([sQuery(id+"F15.wireOp",EDGE,"E155.0.7.0"),sQuery(id+"F15.wireOp",EDGE,"E155.0.7.1"),sQuery(id+"F15.wireOp",EDGE,"E155.0.7.2"),sQuery(id+"F15.wireOp",EDGE,"E155.0.7.3")])]});
            var Q10;
            Q10=makeQuery(id+"F16.opExtrude","SWEPT_BODY",BODY,{"disambiguationData":[OSD([sQuery(id+"F15.wireOp",EDGE,"E155.0.8.0"),sQuery(id+"F15.wireOp",EDGE,"E155.0.8.1"),sQuery(id+"F15.wireOp",EDGE,"E155.0.8.2"),sQuery(id+"F15.wireOp",EDGE,"E155.0.8.3")])]});
            var Q11;
            Q11=makeQuery(id+"F16.opExtrude","SWEPT_BODY",BODY,{"disambiguationData":[OSD([sQuery(id+"F15.wireOp",EDGE,"E155.0.9.0"),sQuery(id+"F15.wireOp",EDGE,"E155.0.9.1"),sQuery(id+"F15.wireOp",EDGE,"E155.0.9.2"),sQuery(id+"F15.wireOp",EDGE,"E155.0.9.3")])]});
            var Q12;
            Q12=qCreatedBy(makeId("Front.planeOp"),FACE);
            mirror(context, id + "F17", {"entities" : qUnion([Q0, Q1, Q2, Q3, Q4, Q5, Q6, Q7, Q8, Q9, Q10, Q11]), "mirrorPlane" : qUnion([Q12])});
        }
    });
